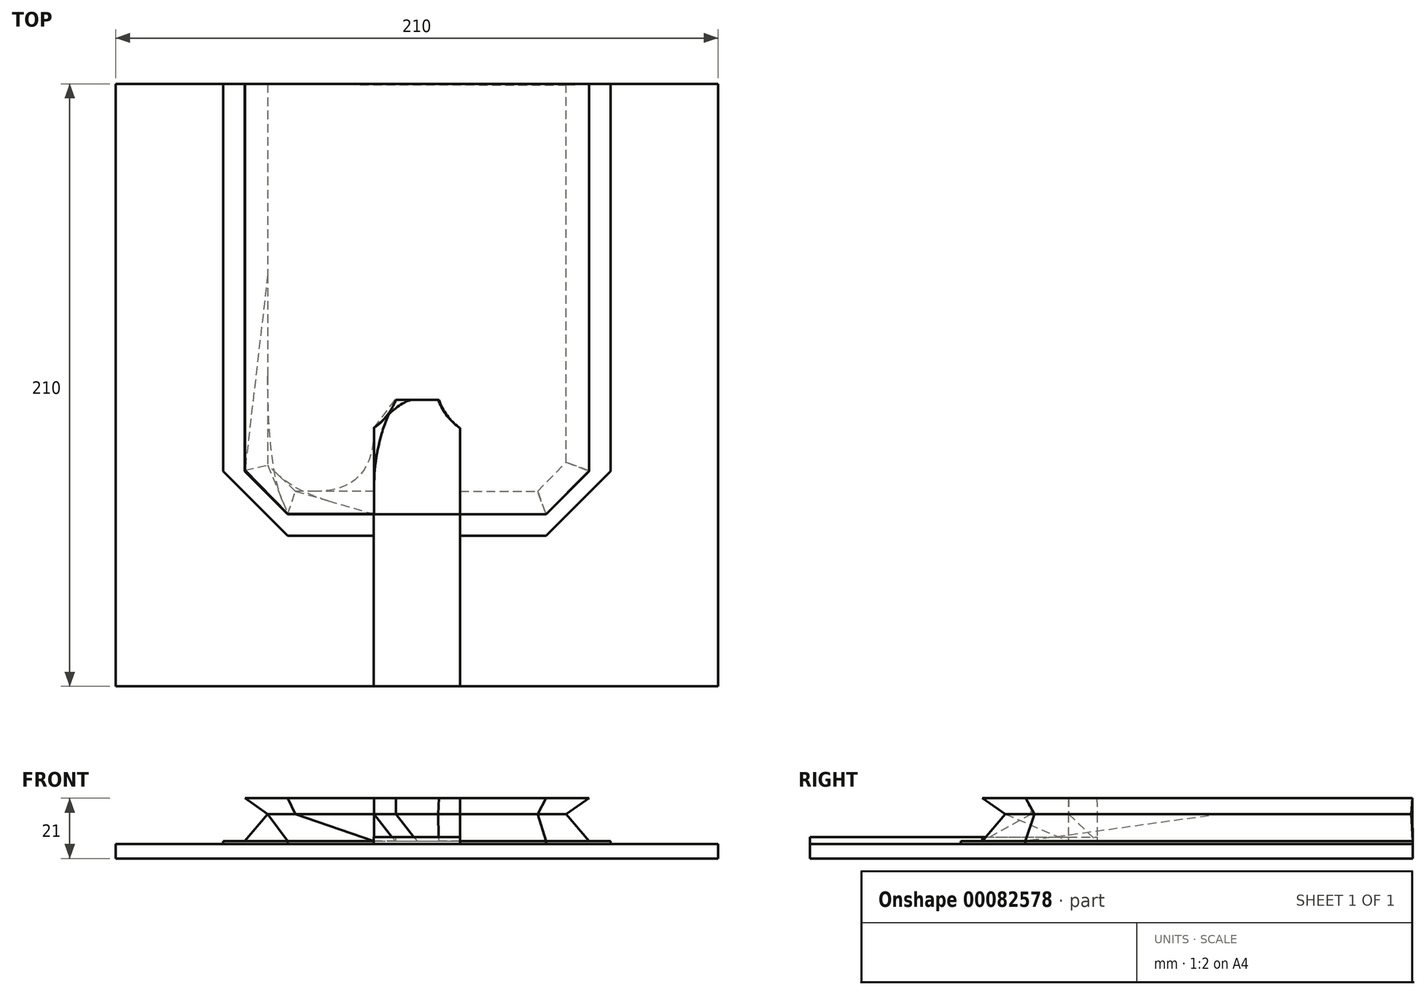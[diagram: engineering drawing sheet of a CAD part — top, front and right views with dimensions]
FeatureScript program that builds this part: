
annotation { "Feature Type Name" : "Feature", "Feature Type Description" : "" }
export const myFeature = defineFeature(function(context is Context, id is Id, definition is map)
    precondition{}
    {
        {
            var Q0;
            Q0=qCreatedBy(makeId("Top.planeOp"),FACE);
            cPlane(context, id + "F0", {"entities" : qUnion([Q0]), "cplaneType" : CPlaneType.OFFSET, "offset" : 70 * mm, "oppositeDirection" : true, "width" : 150 * mm, "height" : 150 * mm});
        }
        {
            var Q0;
            Q0=qCreatedBy(id+"F0.planeOp",FACE);
            var sketch = newSketch(context, id + "F1", { "sketchPlane" : qUnion([Q0])});
            skLineSegment(sketch, "E0.bottom", {"start": v(-107.32, -105.17) * mm, "end": v(102.68, -105.17) * mm});
            skLineSegment(sketch, "E0.top", {"start": v(-107.32, 104.83) * mm, "end": v(102.68, 104.83) * mm});
            skLineSegment(sketch, "E0.left", {"start": v(-107.32, -105.17) * mm, "end": v(-107.32, 104.83) * mm});
            skLineSegment(sketch, "E0.right", {"start": v(102.68, -105.17) * mm, "end": v(102.68, 104.83) * mm});
            skSolve(sketch);
        }
        {
            var Q0;
            Q0 = qSketchRegion(id + "F1", true);
            extrude(context, id + "F2", {"entities" : qUnion([Q0]), "depth" : 5 * mm});
        }
        {
            var Q0;
            Q0=makeQuery(id+"F2.opExtrude","CAP_FACE",FACE,{"disambiguationData":[OSD([sQuery(id+"F1.wireOp",EDGE,"E0.bottom"),sQuery(id+"F1.wireOp",EDGE,"E0.top"),sQuery(id+"F1.wireOp",EDGE,"E0.left"),sQuery(id+"F1.wireOp",EDGE,"E0.right")])],"isStart":false});
            var sketch = newSketch(context, id + "F3", { "sketchPlane" : qUnion([Q0])});
            skLineSegment(sketch, "E1", {"start": v(-17.32, -105.17) * mm, "end": v(12.68, -105.17) * mm});
            skLineSegment(sketch, "E2", {"start": v(-17.32, -105.17) * mm, "end": v(-17.32, -45.17) * mm});
            skLineSegment(sketch, "E3", {"start": v(12.68, -45.17) * mm, "end": v(12.68, -105.17) * mm});
            skLineSegment(sketch, "E4", {"start": v(-62.32, 104.83) * mm, "end": v(57.68, 104.83) * mm});
            skLineSegment(sketch, "E5", {"start": v(12.68, -52.67) * mm, "end": v(42.68, -52.67) * mm});
            skLineSegment(sketch, "E6", {"start": v(65.18, 104.83) * mm, "end": v(65.18, -30.17) * mm});
            skLineSegment(sketch, "E7", {"start": v(65.18, -30.17) * mm, "end": v(42.68, -52.67) * mm});
            skLineSegment(sketch, "E8", {"start": v(-17.32, -52.67) * mm, "end": v(-47.32, -52.67) * mm});
            skLineSegment(sketch, "E9", {"start": v(-47.32, -52.67) * mm, "end": v(-69.82, -30.17) * mm});
            skLineSegment(sketch, "E10", {"start": v(-69.82, -30.17) * mm, "end": v(-69.82, 104.83) * mm});
            skLineSegment(sketch, "E11", {"start": v(-69.82, 104.83) * mm, "end": v(-62.32, 104.83) * mm});
            skLineSegment(sketch, "E12", {"start": v(57.68, 104.83) * mm, "end": v(65.18, 104.83) * mm});
            skSolve(sketch);
        }
        {
            var Q0;
            {var subQ0=sQuery(id+"F3.wireOp",EDGE,"72L8wqU8-EtpD-t0iJ-UvfQ-qKRuMxh7f7UY");Q0=makeQuery(id+"F3.imprint","IMPRINT",FACE,{"disambiguationData":[TD([[makeQuery(id+"F3.imprint","IMPRINT",EDGE,{"derivedFrom":subQ0}),1.0]])]});}
            var Q1;
            Q1=makeQuery(id+"F3.imprint","IMPRINT",FACE,{"disambiguationData":[TD([[makeQuery(id+"F3.imprint","IMPRINT",EDGE,{"derivedFrom":sQuery(id+"F3.wireOp",EDGE,"P01qEWm8-cpiO-Rsgc-mQ5z-jQ03dFQWaqfQ")}),1.0]])]});
            var Q2;
            Q2=makeQuery(id+"F3.imprint","IMPRINT",FACE,{"disambiguationData":[TD([[makeQuery(id+"F3.imprint","IMPRINT",EDGE,{"derivedFrom":sQuery(id+"F3.wireOp",EDGE,"MevUYgB1-DHFj-0HPU-p554-gx0ah0y5PqNS")}),1.0]])]});
            var Q3;
            {var subQ3=sQuery(id+"F3.wireOp",EDGE,"E1");Q3=makeQuery(id+"F3.imprint","IMPRINT",FACE,{"disambiguationData":[TD([[makeQuery(id+"F3.imprint","IMPRINT",EDGE,{"derivedFrom":subQ3}),1.0]])]});}
            var Q4;
            Q4=makeQuery(id+"F3.imprint","IMPRINT",FACE,{"disambiguationData":[TD([[makeQuery(id+"F3.imprint","IMPRINT",EDGE,{"derivedFrom":sQuery(id+"F3.wireOp",EDGE,"72L8wqU8-EtpD-t0iJ-UvfQ-qKRuMxh7f7UY")}),-1.0]])]});
            var Q5;
            Q5 = qSketchRegion(id + "F7", true);
            extrude(context, id + "F4", {"entities" : qUnion([Q0, Q1, Q2, Q3, Q4, Q5]), "depth" : 1 * mm});
        }
        {
            var Q0;
            Q0=makeQuery(id+"F4.opExtrude","CAP_FACE",FACE,{"disambiguationData":[OSD([sQuery(id+"F3.wireOp",EDGE,"E1"),sQuery(id+"F3.wireOp",EDGE,"E2"),sQuery(id+"F3.wireOp",EDGE,"E3"),sQuery(id+"F3.wireOp",EDGE,"E4"),sQuery(id+"F3.wireOp",EDGE,"E5"),sQuery(id+"F3.wireOp",EDGE,"E6"),sQuery(id+"F3.wireOp",EDGE,"E7"),sQuery(id+"F3.wireOp",EDGE,"E8"),sQuery(id+"F3.wireOp",EDGE,"E9"),sQuery(id+"F3.wireOp",EDGE,"E10"),sQuery(id+"F3.wireOp",EDGE,"E11"),sQuery(id+"F3.wireOp",EDGE,"E12")])],"isStart":false});
            var sketch = newSketch(context, id + "F5", { "sketchPlane" : qUnion([Q0])});
            skLineSegment(sketch, "E13", {"start": v(-17.32, -52.67) * mm, "end": v(-17.32, -45.17) * mm});
            skLineSegment(sketch, "E14", {"start": v(-17.32, -45.17) * mm, "end": v(12.68, -45.17) * mm});
            skLineSegment(sketch, "E15", {"start": v(12.68, -45.17) * mm, "end": v(12.68, -105.17) * mm});
            skLineSegment(sketch, "E16", {"start": v(12.68, -105.17) * mm, "end": v(-17.32, -105.17) * mm});
            skLineSegment(sketch, "E17", {"start": v(-17.32, -105.17) * mm, "end": v(-17.32, -52.67) * mm});
            skSolve(sketch);
        }
        {
            var Q0;
            Q0 = qSketchRegion(id + "F5", true);
            extrude(context, id + "F6", {"entities" : qUnion([Q0]), "operationType" : NewBodyOperationType.ADD, "depth" : 1.5 * mm});
        }
        {
            var Q0;
            Q0=makeQuery(id+"F4.opExtrude","CAP_FACE",FACE,{"disambiguationData":[OSD([sQuery(id+"F3.wireOp",EDGE,"E1"),sQuery(id+"F3.wireOp",EDGE,"E2"),sQuery(id+"F3.wireOp",EDGE,"E3"),sQuery(id+"F3.wireOp",EDGE,"E4"),sQuery(id+"F3.wireOp",EDGE,"E5"),sQuery(id+"F3.wireOp",EDGE,"E6"),sQuery(id+"F3.wireOp",EDGE,"E7"),sQuery(id+"F3.wireOp",EDGE,"E8"),sQuery(id+"F3.wireOp",EDGE,"E9"),sQuery(id+"F3.wireOp",EDGE,"E10"),sQuery(id+"F3.wireOp",EDGE,"E11"),sQuery(id+"F3.wireOp",EDGE,"E12")])],"isStart":false});
            var sketch = newSketch(context, id + "F7", { "sketchPlane" : qUnion([Q0])});
            skLineSegment(sketch, "E18", {"start": v(-17.32, -45.17) * mm, "end": v(-47.32, -45.17) * mm});
            skLineSegment(sketch, "E19", {"start": v(-62.32, -30.17) * mm, "end": v(-62.32, 104.83) * mm});
            skLineSegment(sketch, "E20", {"start": v(-62.32, 104.83) * mm, "end": v(57.68, 104.83) * mm});
            skLineSegment(sketch, "E21", {"start": v(57.68, 104.83) * mm, "end": v(57.68, -30.17) * mm});
            skLineSegment(sketch, "E22", {"start": v(12.68, -45.17) * mm, "end": v(42.68, -45.17) * mm});
            skLineSegment(sketch, "E23", {"start": v(42.68, -45.17) * mm, "end": v(57.68, -30.17) * mm});
            skLineSegment(sketch, "E24", {"start": v(-47.32, -45.17) * mm, "end": v(-62.32, -30.17) * mm});
            skLineSegment(sketch, "E25", {"start": v(-17.32, -45.17) * mm, "end": v(-17.32, -15.17) * mm});
            skLineSegment(sketch, "E26", {"start": v(12.68, -45.17) * mm, "end": v(12.68, -15.17) * mm});
            skLineSegment(sketch, "E27", {"start": v(-9.82, -5.17) * mm, "end": v(-2.32, -5.17) * mm});
            skLineSegment(sketch, "E28", {"start": v(-2.32, -5.17) * mm, "end": v(5.18, -5.17) * mm});
            skArc(sketch, "E29", {"start": v(-17.32, -15.17) * mm, "mid": v(-12.77, -10.77) * mm, "end": v(-9.82, -5.17) * mm});
            skArc(sketch, "E30", {"start": v(5.18, -5.17) * mm, "mid": v(8.13, -10.77) * mm, "end": v(12.68, -15.17) * mm});
            skSolve(sketch);
        }
        {
            var Q0;
            Q0=makeQuery(id+"F7.imprint","IMPRINT",FACE,{"disambiguationData":[TD([[makeQuery(id+"F7.imprint","IMPRINT",EDGE,{"derivedFrom":sQuery(id+"F7.wireOp",EDGE,"E18")}),-1.0]])]});
            cPlane(context, id + "F8", {"entities" : qUnion([Q0]), "cplaneType" : CPlaneType.OFFSET, "offset" : 9.5 * mm, "width" : 150 * mm, "height" : 150 * mm});
        }
        {
            var Q0;
            Q0=qCreatedBy(id+"F8.planeOp",FACE);
            var sketch = newSketch(context, id + "F9", { "sketchPlane" : qUnion([Q0])});
            skLineSegment(sketch, "E31", {"start": v(-54.32, 104.67) * mm, "end": v(-54.32, -28.03) * mm});
            skLineSegment(sketch, "E32", {"start": v(-17.27, -37.17) * mm, "end": v(-44.64, -37.17) * mm});
            skLineSegment(sketch, "E33", {"start": v(-44.64, -37.17) * mm, "end": v(-54.32, -28.03) * mm});
            skLineSegment(sketch, "E34", {"start": v(-17.27, -37.17) * mm, "end": v(-17.27, -15.06) * mm});
            skLineSegment(sketch, "E35", {"start": v(12.76, -37.17) * mm, "end": v(12.76, -15.2) * mm});
            skLineSegment(sketch, "E36", {"start": v(12.76, -37.17) * mm, "end": v(39.74, -37.17) * mm});
            skLineSegment(sketch, "E37", {"start": v(39.74, -37.17) * mm, "end": v(49.68, -27.05) * mm});
            skLineSegment(sketch, "E38", {"start": v(49.68, -27.05) * mm, "end": v(49.68, 104.38) * mm});
            skLineSegment(sketch, "E39", {"start": v(-54.32, 104.67) * mm, "end": v(49.68, 104.38) * mm});
            skArc(sketch, "E40", {"start": v(-17.27, -15.06) * mm, "mid": v(-12.67, -10.7) * mm, "end": v(-9.66, -5.14) * mm});
            skArc(sketch, "E41", {"start": v(5.09, -5.14) * mm, "mid": v(8.1, -10.8) * mm, "end": v(12.76, -15.2) * mm});
            skLineSegment(sketch, "E42", {"start": v(-9.66, -5.14) * mm, "end": v(5.09, -5.14) * mm});
            skSolve(sketch);
        }
        {
            var Q1;
            Q1=makeQuery(id+"F9.imprint","IMPRINT",FACE,{"disambiguationData":[TD([[makeQuery(id+"F9.imprint","IMPRINT",EDGE,{"derivedFrom":sQuery(id+"F9.wireOp",EDGE,"E31")}),1.0]])]});
            var Q2;
            Q2=makeQuery(id+"F7.imprint","IMPRINT",FACE,{"disambiguationData":[TD([[makeQuery(id+"F7.imprint","IMPRINT",EDGE,{"derivedFrom":sQuery(id+"F7.wireOp",EDGE,"E18")}),-1.0]])]});
            loft(context, id + "F10", {"operationType" : NewBodyOperationType.ADD, "sheetProfilesArray" : [{ "sheetProfileEntities" : qUnion([Q1]) }, { "sheetProfileEntities" : qUnion([Q2]) }]});
        }
        {
            var Q0;
            Q0=qCreatedBy(id+"F8.planeOp",FACE);
            cPlane(context, id + "F11", {"entities" : qUnion([Q0]), "cplaneType" : CPlaneType.OFFSET, "offset" : 5.5 * mm, "width" : 150 * mm, "height" : 150 * mm});
        }
        {
            var Q0;
            Q0=qCreatedBy(id+"F11.planeOp",FACE);
            var sketch = newSketch(context, id + "F12", { "sketchPlane" : qUnion([Q0])});
            skLineSegment(sketch, "E43", {"start": v(-17.26, -45.12) * mm, "end": v(-17.26, -14.98) * mm});
            skLineSegment(sketch, "E44", {"start": v(-17.26, -45.12) * mm, "end": v(-47.31, -45.12) * mm});
            skLineSegment(sketch, "E45", {"start": v(-47.31, -45.12) * mm, "end": v(-62.24, -29.83) * mm});
            skLineSegment(sketch, "E46", {"start": v(-62.24, -29.83) * mm, "end": v(-62.24, 104.76) * mm});
            skLineSegment(sketch, "E47", {"start": v(-62.24, 104.76) * mm, "end": v(57.69, 104.76) * mm});
            skLineSegment(sketch, "E48", {"start": v(57.69, 104.76) * mm, "end": v(57.69, -30.04) * mm});
            skLineSegment(sketch, "E49", {"start": v(57.69, -30.04) * mm, "end": v(42.68, -45.15) * mm});
            skLineSegment(sketch, "E50", {"start": v(42.68, -45.15) * mm, "end": v(12.76, -45.15) * mm});
            skLineSegment(sketch, "E51", {"start": v(12.76, -45.15) * mm, "end": v(12.76, -15.21) * mm});
            skArc(sketch, "E52", {"start": v(-17.26, -14.98) * mm, "mid": v(-12.69, -10.73) * mm, "end": v(-9.65, -5.27) * mm});
            skArc(sketch, "E53", {"start": v(5.32, -5.26) * mm, "mid": v(8.25, -10.83) * mm, "end": v(12.76, -15.21) * mm});
            skLineSegment(sketch, "E54", {"start": v(-9.65, -5.27) * mm, "end": v(5.32, -5.26) * mm});
            skSolve(sketch);
        }
        {
            var Q1;
            Q1=makeQuery(id+"F12.imprint","IMPRINT",FACE,{"disambiguationData":[TD([[makeQuery(id+"F12.imprint","IMPRINT",EDGE,{"derivedFrom":sQuery(id+"F12.wireOp",EDGE,"E43")}),1.0]])]});
            var Q2;
            Q2=makeQuery(id+"F10.opLoft","CAP_FACE",FACE,{"disambiguationData":[OSD([makeQuery(id+"F9.imprint","IMPRINT",FACE,{"disambiguationData":[TD([[makeQuery(id+"F9.imprint","IMPRINT",EDGE,{"derivedFrom":sQuery(id+"F9.wireOp",EDGE,"E31")}),1.0]])]})])],"isStart":true});
            loft(context, id + "F13", {"operationType" : NewBodyOperationType.ADD, "sheetProfilesArray" : [{ "sheetProfileEntities" : qUnion([Q1]) }, { "sheetProfileEntities" : qUnion([Q2]) }]});
        }
        {
            var Q0;
            {var subQ10=sQuery(id+"F9.wireOp",EDGE,"E34");var subQ12=sQuery(id+"F7.wireOp",EDGE,"E25");var subQ14=sQuery(id+"F3.wireOp",EDGE,"E3");var subQ15=sQuery(id+"F3.wireOp",EDGE,"E2");var subQ16=makeQuery(id+"F4.opExtrude","CAP_FACE",FACE,{"disambiguationData":[OSD([sQuery(id+"F3.wireOp",EDGE,"E1"),subQ15,subQ14,sQuery(id+"F3.wireOp",EDGE,"E4"),sQuery(id+"F3.wireOp",EDGE,"E5"),sQuery(id+"F3.wireOp",EDGE,"E6"),sQuery(id+"F3.wireOp",EDGE,"E7"),sQuery(id+"F3.wireOp",EDGE,"E8"),sQuery(id+"F3.wireOp",EDGE,"E9"),sQuery(id+"F3.wireOp",EDGE,"E10"),sQuery(id+"F3.wireOp",EDGE,"E11"),sQuery(id+"F3.wireOp",EDGE,"E12")])],"isStart":false});var subQ17=sQuery(id+"F9.wireOp",EDGE,"E42");var subQ18=sQuery(id+"F9.wireOp",EDGE,"E40");var subQ19=sQuery(id+"F7.wireOp",EDGE,"E29");var subQ20=sQuery(id+"F7.wireOp",EDGE,"E27");Q0=makeQuery(id+"F10.boolean.opBoolean","SPLIT",FACE,{"disambiguationData":[TD([makeQuery(id+"F10.opLoft","SWEPT_FACE",FACE,{"disambiguationData":[OSD([subQ12,subQ20,subQ19,subQ10,subQ18,subQ17])]})])],"derivedFrom":subQ16});}
            var sketch = newSketch(context, id + "F14", { "sketchPlane" : qUnion([Q0])});
            skLineSegment(sketch, "E55", {"start": v(-17.32, -45.17) * mm, "end": v(-17.32, -15.17) * mm});
            skLineSegment(sketch, "E56", {"start": v(12.68, -45.17) * mm, "end": v(-17.32, -45.17) * mm});
            skLineSegment(sketch, "E57", {"start": v(12.68, -45.17) * mm, "end": v(12.68, -15.17) * mm});
            skLineSegment(sketch, "E58", {"start": v(-9.82, -5.17) * mm, "end": v(5.18, -5.17) * mm});
            skArc(sketch, "E59", {"start": v(-17.32, -15.17) * mm, "mid": v(-12.77, -10.77) * mm, "end": v(-9.82, -5.17) * mm});
            skArc(sketch, "E60", {"start": v(5.18, -5.17) * mm, "mid": v(8.13, -10.77) * mm, "end": v(12.68, -15.17) * mm});
            skSolve(sketch);
        }
        {
            var Q0;
            Q0 = qSketchRegion(id + "F14", true);
            extrude(context, id + "F15", {"entities" : qUnion([Q0]), "depth" : 1.5 * mm});
        }
    });
